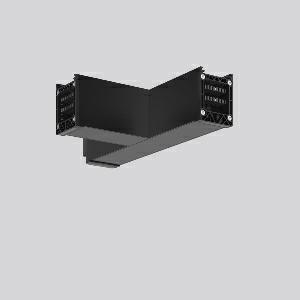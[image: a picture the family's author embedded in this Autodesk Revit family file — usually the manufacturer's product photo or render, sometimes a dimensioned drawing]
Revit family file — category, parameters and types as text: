
# Revit family: linedo_t-verbindung_982774_003_5_b931
name_source: partatom
category: Lighting Fixtures
units: mm (PartAtom-declared; Revit-internal decimal feet)

## family parameters
Cut with Voids When Loaded = No
Host = Face
Light Source = No
Part Type = Normal
Room Calculation Point = No
Round Connector Dimension = Use Diameter
Shared = No

## types (1)
- LINEDO T-Verbindung
    Apparent Load = 0 VA
    Default Elevation = 1800 mm
    Description = Series: LINEDO
T-connector, 7-pole, connection socket / plug - socket. Housing: extruded aluminium profile, powder-coated. Cover made of plastic, surface like housing. LINEDO plug system, plastic, black. Easy connection for rigid or flexible wires. 5 membrane cable entries (2 x M20 and 3 x M25). Suitable for power supply in 7-pole version. Ready prewired. Colour-coded individual cables enable easy electromechanical separation.
Colour: jet black (RAL 9005)
Length: 330 mm
Width: 185 mm
Height: 76 mm
Weight: 940 g
    Height = 76 mm
    Lamp = 0 x
    Length = 331 mm
    Luminous efficacy = 0 lm/W
    Manufacturer = RZB
    ModVariant = No
    Model = 982774.003.5
    Mounting Place = Ceiling
    Mounting Type = Surface mounted
    Number of Poles = 1
    OnlyDefault = Yes
    Power Factor = 1
    Product Name = LINEDO T-Verbindung
    Product group = Surface mounted continuous line luminaire system
    ProductGroupID = 310
    Protection Class = Protection class I
    Protection Degree = Degree of protection
    RLX_Detail_Level = 1
    RLX_Emergency_Light_Flux = 0 lm
    RLX_Emergency_Type = 0
    RLX_Emergency_Type_DB = No
    RlxData = <blob elided: 19869 chars, md5=5a2ff870>
    Standby Power = 0 W
    System Light Flux = 0 lm
    System Power = 0 W
    Type Comments = Product without accessories
    Type Image = 982774.003.1.jpg
    URL = http://relux.com
    VarID = ---
    Voltage = 0 V
    Weight = 0.00 kg
    Width = 185 mm

## geometry (parser evidence)
native form markers: Blend x4, Sweep x11
no freeform markers — native parametric forms only
